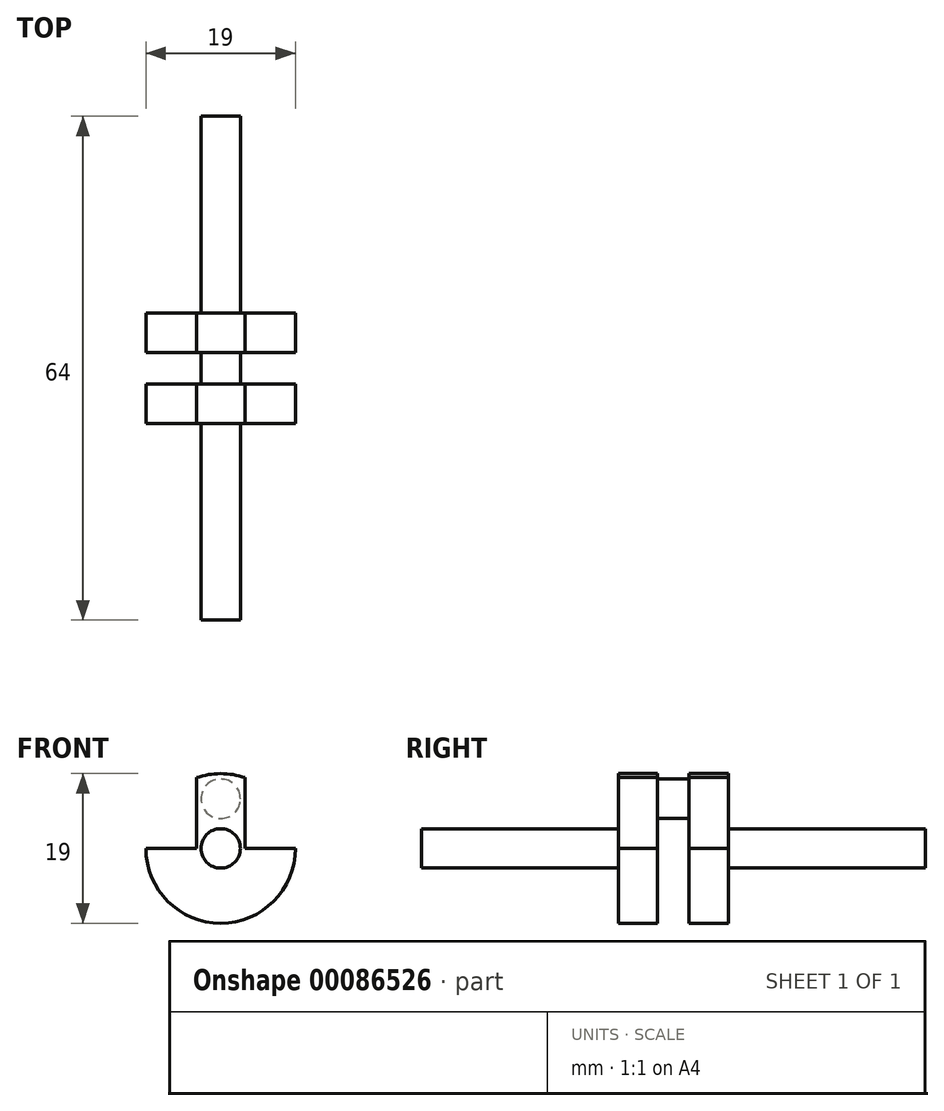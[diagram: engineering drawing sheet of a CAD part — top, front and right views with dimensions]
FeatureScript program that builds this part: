
annotation { "Feature Type Name" : "Feature", "Feature Type Description" : "" }
export const myFeature = defineFeature(function(context is Context, id is Id, definition is map)
    precondition{}
    {
        {
            var Q0;
            Q0=qCreatedBy(makeId("Front.planeOp"),FACE);
            var sketch = newSketch(context, id + "F0", { "sketchPlane" : qUnion([Q0])});
            skPoint(sketch, "E0", {"position": v(0, 6.3) * mm});
            skLineSegment(sketch, "E1.left", {"start": v(3.08, -8.99) * mm, "end": v(3.08, 8.99) * mm});
            skLineSegment(sketch, "E1.right", {"start": v(-3.08, -8.99) * mm, "end": v(-3.08, 8.99) * mm});
            skPoint(sketch, "E1.middle", {"position": v(0, 0) * mm});
            skArc(sketch, "E2", {"start": v(-3.08, 8.99) * mm, "mid": v(0, 9.5) * mm, "end": v(3.08, 8.99) * mm});
            skPoint(sketch, "E3", {"position": v(0, 9.5) * mm});
            skArc(sketch, "E4", {"start": v(3.08, 8.99) * mm, "mid": v(0, 9.5) * mm, "end": v(-3.08, 8.99) * mm});
            skLineSegment(sketch, "E5", {"start": v(3.08, 0) * mm, "end": v(9.5, 0) * mm});
            skLineSegment(sketch, "E6", {"start": v(-3.08, 0) * mm, "end": v(-9.5, 0) * mm});
            skArc(sketch, "E7.trimOffspring", {"start": v(-9.5, 0) * mm, "mid": v(0, -9.5) * mm, "end": v(9.5, 0) * mm});
            skSolve(sketch);
        }
        {
            var Q0;
            Q0=makeQuery(id+"F0.imprint","IMPRINT",FACE,{"disambiguationData":[TD([[makeQuery(id+"F0.imprint","IMPRINT",EDGE,{"derivedFrom":sQuery(id+"F0.wireOp",EDGE,"E1.left")}),1.0]])]});
            var Q1;
            Q1=qSketchRegion(id+"F2",true);
            var Q2;
            {var subQ3=sQuery(id+"F0.wireOp",EDGE,"E6");Q2=makeQuery(id+"F0.imprint","IMPRINT",FACE,{"disambiguationData":[TD([[makeQuery(id+"F0.imprint","IMPRINT",EDGE,{"derivedFrom":subQ3}),1.0]])]});}
            var Q3;
            {var subQ3=sQuery(id+"F0.wireOp",EDGE,"E5");Q3=makeQuery(id+"F0.imprint","IMPRINT",FACE,{"disambiguationData":[TD([[makeQuery(id+"F0.imprint","IMPRINT",EDGE,{"derivedFrom":subQ3}),-1.0]])]});}
            extrude(context, id + "F1", {"entities" : qUnion([Q0, Q1, Q2, Q3]), "depth" : 5 * mm, "symmetric" : true});
        }
        {
            var Q0;
            Q0=makeQuery(id+"F1.opExtrude","CAP_FACE",FACE,{"disambiguationData":[OSD([sQuery(id+"F0.wireOp",EDGE,"E1.left"),sQuery(id+"F0.wireOp",EDGE,"E1.right"),sQuery(id+"F0.wireOp",EDGE,"E2"),sQuery(id+"F0.wireOp",EDGE,"VFhB1kta-8bxy-pE8t-JsMO-NGhGx0J8nSL1")])],"isStart":false});
            var sketch = newSketch(context, id + "F2", { "sketchPlane" : qUnion([Q0])});
            skPoint(sketch, "E8", {"position": v(0, 0) * mm});
            skPoint(sketch, "E9", {"position": v(0, 6.3) * mm});
            skCircle(sketch, "E10", {"center": v(0, 6.3) * mm, "radius": 2.5 * mm});
            skCircle(sketch, "E11", {"center": v(0, 0) * mm, "radius": 2.5 * mm});
            skSolve(sketch);
        }
        {
            var Q0;
            Q0=makeQuery(id+"F1.opExtrude","SWEPT_BODY",BODY,{"disambiguationData":[OSD([sQuery(id+"F0.wireOp",EDGE,"E1.left"),sQuery(id+"F0.wireOp",EDGE,"E1.right"),sQuery(id+"F0.wireOp",EDGE,"E2"),sQuery(id+"F0.wireOp",EDGE,"VFhB1kta-8bxy-pE8t-JsMO-NGhGx0J8nSL1")])]});
            transform(context, id + "F3", {"entities" : qUnion([Q0]), "transformType" : TransformType.TRANSLATION_3D, "dx" : 0 * mm, "dy" : 9 * mm, "dz" : 0 * mm, "makeCopy" : true});
        }
        {
            var Q0;
            Q0=makeQuery(id+"F2.imprint","IMPRINT",FACE,{"disambiguationData":[TD([[makeQuery(id+"F2.imprint","IMPRINT",EDGE,{"derivedFrom":sQuery(id+"F2.wireOp",EDGE,"E10")}),1.0]])]});
            var Q1;
            Q1=sQuery(id+"F2.wireOp",EDGE,"E10");
            var Q2;
            Q2=makeQuery(id+"F3.opPattern","COPY",FACE,{"derivedFrom":makeQuery(id+"F1.opExtrude","CAP_FACE",FACE,{"disambiguationData":[OSD([sQuery(id+"F0.wireOp",EDGE,"E1.left"),sQuery(id+"F0.wireOp",EDGE,"E1.right"),sQuery(id+"F0.wireOp",EDGE,"E2"),sQuery(id+"F0.wireOp",EDGE,"VFhB1kta-8bxy-pE8t-JsMO-NGhGx0J8nSL1")])],"isStart":true}),"instanceName":"1"});
            extrude(context, id + "F4", {"entities" : qUnion([Q0]), "operationType" : NewBodyOperationType.ADD, "surfaceEntities" : qUnion([Q1]), "endBound" : BoundingType.UP_TO_SURFACE, "oppositeDirection" : true, "endBoundEntityFace" : qUnion([Q2]), "depth" : 25 * mm});
        }
        {
            var Q0;
            Q0=makeQuery(id+"F1.opExtrude","CAP_FACE",FACE,{"disambiguationData":[OSD([sQuery(id+"F0.wireOp",EDGE,"E1.left"),sQuery(id+"F0.wireOp",EDGE,"E1.right"),sQuery(id+"F0.wireOp",EDGE,"E2"),sQuery(id+"F0.wireOp",EDGE,"VFhB1kta-8bxy-pE8t-JsMO-NGhGx0J8nSL1")])],"isStart":true});
            var sketch = newSketch(context, id + "F5", { "sketchPlane" : qUnion([Q0])});
            skCircle(sketch, "E12", {"center": v(0, 0) * mm, "radius": 2.5 * mm});
            skSolve(sketch);
        }
        {
            var Q0;
            Q0=makeQuery(id+"F5.imprint","IMPRINT",FACE,{"disambiguationData":[TD([[makeQuery(id+"F5.imprint","IMPRINT",EDGE,{"derivedFrom":sQuery(id+"F5.wireOp",EDGE,"E12")}),1.0]])]});
            extrude(context, id + "F6", {"entities" : qUnion([Q0]), "operationType" : NewBodyOperationType.ADD, "oppositeDirection" : true, "depth" : 30 * mm});
        }
        {
            var Q0;
            Q0=makeQuery(id+"F3.opPattern","COPY",FACE,{"derivedFrom":makeQuery(id+"F1.opExtrude","CAP_FACE",FACE,{"disambiguationData":[OSD([sQuery(id+"F0.wireOp",EDGE,"E1.left"),sQuery(id+"F0.wireOp",EDGE,"E1.right"),sQuery(id+"F0.wireOp",EDGE,"E2"),sQuery(id+"F0.wireOp",EDGE,"VFhB1kta-8bxy-pE8t-JsMO-NGhGx0J8nSL1")])],"isStart":false}),"instanceName":"1"});
            var sketch = newSketch(context, id + "F7", { "sketchPlane" : qUnion([Q0])});
            skCircle(sketch, "E13", {"center": v(0, 0) * mm, "radius": 2.5 * mm});
            skSolve(sketch);
        }
        {
            var Q0;
            Q0=makeQuery(id+"F7.imprint","IMPRINT",FACE,{"disambiguationData":[TD([[makeQuery(id+"F7.imprint","IMPRINT",EDGE,{"derivedFrom":sQuery(id+"F7.wireOp",EDGE,"E13")}),1.0]])]});
            extrude(context, id + "F8", {"entities" : qUnion([Q0]), "operationType" : NewBodyOperationType.ADD, "oppositeDirection" : true, "depth" : 30 * mm});
        }
    });
